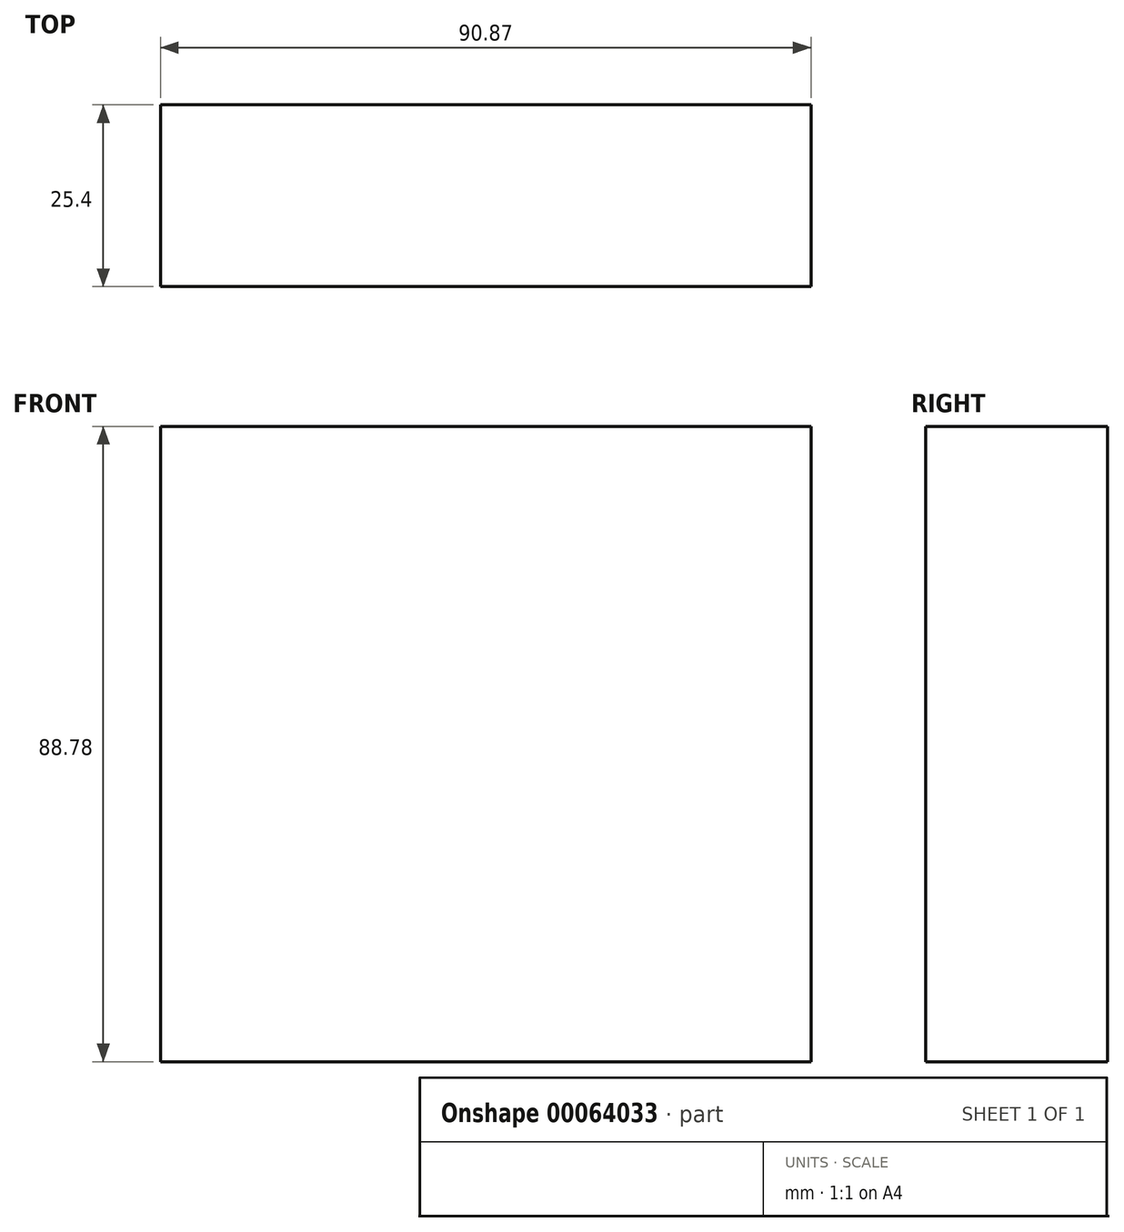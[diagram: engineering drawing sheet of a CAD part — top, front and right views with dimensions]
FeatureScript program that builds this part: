
annotation { "Feature Type Name" : "Feature", "Feature Type Description" : "" }
export const myFeature = defineFeature(function(context is Context, id is Id, definition is map)
    precondition{}
    {
        {
            var Q0;
            Q0=qCreatedBy(makeId("Front.planeOp"),FACE);
            var sketch = newSketch(context, id + "F0", { "sketchPlane" : qUnion([Q0])});
            skLineSegment(sketch, "E0.bottom", {"start": v(-36.65, -38.13) * mm, "end": v(54.22, -38.13) * mm});
            skLineSegment(sketch, "E0.top", {"start": v(-36.65, 50.65) * mm, "end": v(54.22, 50.65) * mm});
            skLineSegment(sketch, "E0.left", {"start": v(-36.65, -38.13) * mm, "end": v(-36.65, 50.65) * mm});
            skLineSegment(sketch, "E0.right", {"start": v(54.22, -38.13) * mm, "end": v(54.22, 50.65) * mm});
            skSolve(sketch);
        }
        {
            var Q0;
            Q0=makeQuery(id+"F0.imprint","IMPRINT",FACE,{"disambiguationData":[TD([[makeQuery(id+"F0.imprint","IMPRINT",EDGE,{"derivedFrom":sQuery(id+"F0.wireOp",EDGE,"E0.bottom")}),1.0]])]});
            extrude(context, id + "F1", {"entities" : qUnion([Q0]), "depth" : 25.4 * mm});
        }
    });
